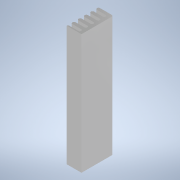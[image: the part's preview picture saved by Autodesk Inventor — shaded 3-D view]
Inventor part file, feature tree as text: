
AUTODESK INVENTOR PART (.ipt)
format: ipt  version: 2020 (Build 240168000, 168)  size: 277,504 bytes
history: native  units: mm
features: fillet x7, extrude x4, sketch x4, other x2, pattern_linear x1
ambient origin geometry x8: Origin, YZ Plane, XZ Plane, XY Plane, X Axis, Y Axis, Z Axis, Center Point
bodies: Body1 (feature_tree)
feature tree (18):
  other  "Bryła1"
  extrude  "Wyciągnięcie proste1"  Depth=5.0mm
  extrude  "Wyciągnięcie proste2"  Depth=1.0mm
  pattern_linear  "Szyk prostokątny1"  Count1=10 Spacing1=0.0mm
  fillet  "Zaokrąglenie1"  Radius=2.0mm
  fillet  "Zaokrąglenie2"  Radius=2.0mm
  fillet  "Zaokrąglenie3"  Radius=2.0mm
  fillet  "Zaokrąglenie4"  Radius=100.0mm
  fillet  "Zaokrąglenie5"  Radius=4.15mm
  fillet  "Zaokrąglenie6"  Radius=1.0mm
  fillet  "Zaokrąglenie7"  Radius=1.0mm
  other  "Pogrubienie1"
  extrude  "Extrusion3"  Depth=1.0mm
  extrude  "Extrusion4"  Depth=1.0mm
  sketch  "Szkic1"
  sketch  "Szkic2"
  sketch  "Sketch3"  dims[d0=10.0mm d1=5.0mm]
  sketch  "Sketch4"  dims[d2=60.0mm d3=30.0mm d4=100.0mm d5=0.0mm d6=2.0mm d7=2.0mm d8=2.0mm d9=100.0mm d10=0.0mm d11=140.0mm d13=4.15mm d14=1.0mm d15=1.0mm d16=1.0mm d17=1.0mm d18=1.0mm d19=1.0mm d20=1.0mm d21=19.0mm d22=19.0mm d23=38.5mm d24=0.0mm d25=30.0mm d26=0.0mm]
